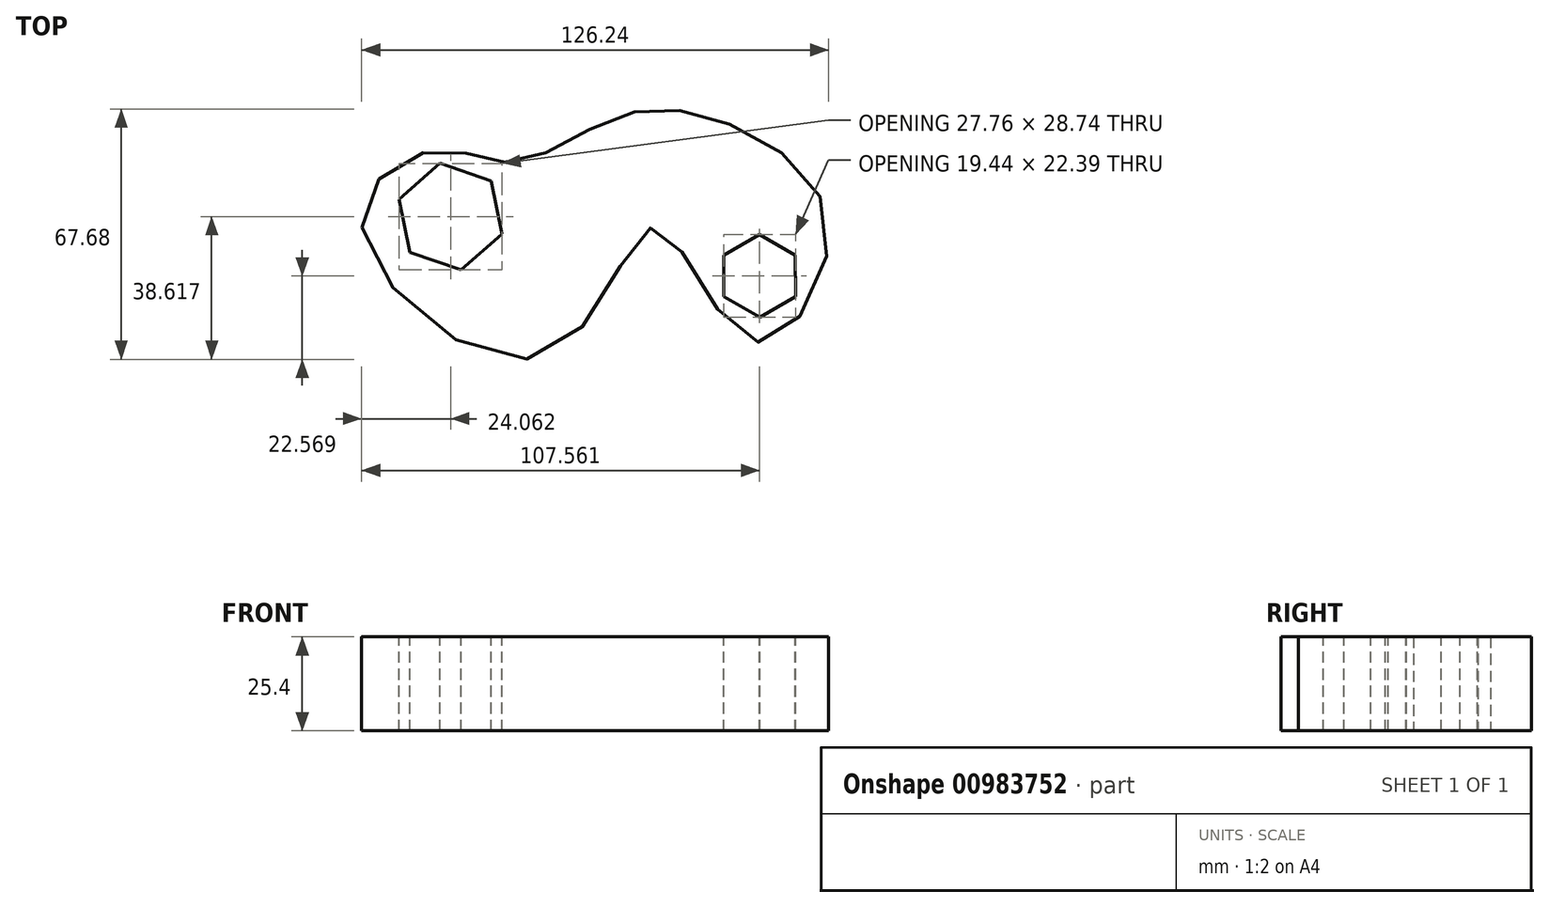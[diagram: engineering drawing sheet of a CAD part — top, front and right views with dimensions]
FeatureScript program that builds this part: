
annotation { "Feature Type Name" : "Feature", "Feature Type Description" : "" }
export const myFeature = defineFeature(function(context is Context, id is Id, definition is map)
    precondition{}
    {
        {
            var Q0;
            Q0=qCreatedBy(makeId("Top.planeOp"),FACE);
            var sketch = newSketch(context, id + "F0", { "sketchPlane" : qUnion([Q0])});
            skFitSpline(sketch, "E0", {"points": [v(-61.98, 0) * mm, v(-12.21, -34.54) * mm, v(17.33, 0) * mm, v(43.61, -30.82) * mm, v(64.08, 0) * mm, v(35, 28.72) * mm, v(6.4, 29.65) * mm, v(-20.82, 17.56) * mm, v(-41.98, 20.82) * mm, v(-61.98, 0) * mm]});
            skSolve(sketch);
        }
        {
            var Q0;
            Q0=makeQuery(id+"F0.imprint","IMPRINT",FACE,{"disambiguationData":[TD([[makeQuery(id+"F0.imprint","IMPRINT",EDGE,{"derivedFrom":sQuery(id+"F0.wireOp",EDGE,"E0")}),1.0]])]});
            extrude(context, id + "F1", {"entities" : qUnion([Q0]), "depth" : 25.4 * mm, "offsetDistance" : 25.4 * mm});
        }
        {
            var Q0;
            Q0=makeQuery(id+"F1.opExtrude","CAP_FACE",FACE,{"disambiguationData":[OSD([sQuery(id+"F0.wireOp",EDGE,"E0")])],"isStart":false});
            var sketch = newSketch(context, id + "F2", { "sketchPlane" : qUnion([Q0])});
            skCircle(sketch, "E1.cCircle", {"center": v(-38.03, 2.9) * mm, "radius": 12.7 * mm, "construction": true});
            skLineSegment(sketch, "E1.0", {"start": v(-24.15, -1.8) * mm, "end": v(-35.16, -11.46) * mm});
            skLineSegment(sketch, "E1.1", {"start": v(-35.16, -11.46) * mm, "end": v(-49.04, -6.76) * mm});
            skLineSegment(sketch, "E1.2", {"start": v(-49.04, -6.76) * mm, "end": v(-51.9, 7.6) * mm});
            skLineSegment(sketch, "E1.3", {"start": v(-51.9, 7.6) * mm, "end": v(-40.9, 17.28) * mm});
            skLineSegment(sketch, "E1.4", {"start": v(-40.9, 17.28) * mm, "end": v(-27.02, 12.58) * mm});
            skLineSegment(sketch, "E1.5", {"start": v(-27.02, 12.58) * mm, "end": v(-24.15, -1.8) * mm});
            skPoint(sketch, "E1.0.midPoint", {"position": v(-29.65, -6.63) * mm});
            skSolve(sketch);
        }
        {
            var Q0;
            Q0=makeQuery(id+"F2.imprint","IMPRINT",FACE,{"disambiguationData":[TD([[makeQuery(id+"F2.imprint","IMPRINT",EDGE,{"derivedFrom":sQuery(id+"F2.wireOp",EDGE,"E1.0")}),-1.0]])]});
            extrude(context, id + "F3", {"entities" : qUnion([Q0]), "operationType" : NewBodyOperationType.REMOVE, "oppositeDirection" : true, "depth" : 53.6 * mm, "offsetDistance" : 25.4 * mm});
        }
        {
            var Q0;
            Q0=makeQuery(id+"F1.opExtrude","CAP_FACE",FACE,{"disambiguationData":[OSD([sQuery(id+"F0.wireOp",EDGE,"E0")])],"isStart":false});
            var sketch = newSketch(context, id + "F4", { "sketchPlane" : qUnion([Q0])});
            skCircle(sketch, "E2.cCircle", {"center": v(45.47, -13.14) * mm, "radius": 9.7 * mm, "construction": true});
            skLineSegment(sketch, "E2.0", {"start": v(35.75, -7.59) * mm, "end": v(45.42, -1.95) * mm});
            skLineSegment(sketch, "E2.1", {"start": v(45.42, -1.95) * mm, "end": v(55.14, -7.5) * mm});
            skLineSegment(sketch, "E2.2", {"start": v(55.14, -7.5) * mm, "end": v(55.19, -18.7) * mm});
            skLineSegment(sketch, "E2.3", {"start": v(55.19, -18.7) * mm, "end": v(45.52, -24.33) * mm});
            skLineSegment(sketch, "E2.4", {"start": v(45.52, -24.33) * mm, "end": v(35.8, -18.78) * mm});
            skLineSegment(sketch, "E2.5", {"start": v(35.8, -18.78) * mm, "end": v(35.75, -7.59) * mm});
            skPoint(sketch, "E2.0.midPoint", {"position": v(40.59, -4.77) * mm});
            skSolve(sketch);
        }
        {
            var Q0;
            Q0=makeQuery(id+"F4.imprint","IMPRINT",FACE,{"disambiguationData":[TD([[makeQuery(id+"F4.imprint","IMPRINT",EDGE,{"derivedFrom":sQuery(id+"F4.wireOp",EDGE,"E2.0")}),-1.0]])]});
            extrude(context, id + "F5", {"entities" : qUnion([Q0]), "operationType" : NewBodyOperationType.REMOVE, "oppositeDirection" : true, "depth" : 46.74 * mm, "offsetDistance" : 25.4 * mm});
        }
    });
